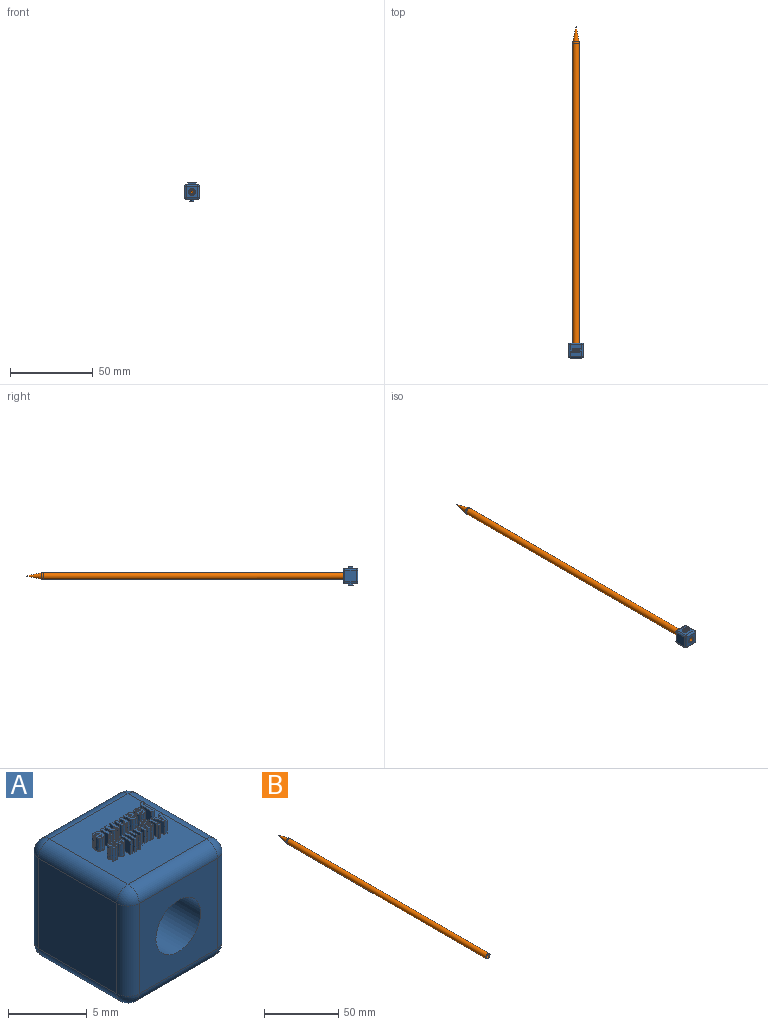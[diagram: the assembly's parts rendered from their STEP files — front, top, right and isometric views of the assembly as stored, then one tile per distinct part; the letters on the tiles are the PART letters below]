
ASSEMBLY  parts=2 mates=1
PART A: 336 faces, bbox 9x9x11 mm
  f0: plane 7x7mm, normal (0,0,1), area 44.8mm2, adj f7,f8,f9,f10,f11,f12,f13,f14
  f1: plane 7x7mm, normal (0,0,-1), area 44.5mm2, adj f136,f140,f141,f142,f162,f163,f164,f165
  f2: plane 7x7mm, normal (-1,0,0), area 49mm2, adj f141,f150,f151,f155
  f3: plane 7x7mm, normal (1,0,0), area 49mm2, adj f136,f139,f143,f144
  f4: plane 7x7mm, normal (0,-1,0), area 36.4mm2, adj f6,f139,f140,f149,f150
  f5: plane 7x7mm, normal (0,1,0), area 36.4mm2, adj f6,f142,f143,f151,f152
  f6: cylinder r=2mm len=9mm, axis (0,-1,0), area 113.1mm2, adj f4,f5
  f7: extruded ~1x0.12mm, area 0.1mm2, adj f0,f8,f16,f17
  f8: extruded ~1x0.22mm, area 0.2mm2, adj f0,f7,f9,f17
  f9: extruded ~1x0.25mm, area 0.3mm2, adj f0,f8,f10,f17
  f10: plane 1x0.87mm, normal (-1,0,0), area 0.9mm2, adj f0,f9,f11,f17
  f11: plane 1x0.2mm, normal (0,-1,0), area 0.2mm2, adj f0,f10,f12,f17
  f12: plane 1x0.87mm, normal (1,0,0), area 0.9mm2, adj f0,f11,f13,f17
  f13: extruded ~1x0.13mm, area 0.1mm2, adj f0,f12,f14,f17
  f14: extruded ~1x0.09mm, area 0.1mm2, adj f0,f13,f15,f17
  f15: extruded ~1x0.09mm, area 0.1mm2, adj f0,f14,f16,f17
  f16: plane 1x0.16mm, normal (1,0,0), area 0.2mm2, adj f0,f7,f15,f17
  f17: plane 1.21x0.41mm, normal (0,0,1), area 0.3mm2, adj f7,f8,f9,f10,f11,f12,f13,f14
  f18: extruded ~1x0.27mm, area 0.3mm2, adj f0,f19,f37,f38
  f19: extruded ~1x0.14mm, area 0.1mm2, adj f0,f18,f20,f38
  f20: extruded ~1x0.11mm, area 0.1mm2, adj f0,f19,f21,f38
  f21: plane 1x0.15mm, normal (-1,0,0), area 0.2mm2, adj f0,f20,f22,f38
  f22: extruded ~1x0.12mm, area 0.1mm2, adj f0,f21,f23,f38
  f23: extruded ~1x0.12mm, area 0.1mm2, adj f0,f22,f24,f38
  f24: extruded ~1x0.13mm, area 0.1mm2, adj f0,f23,f25,f38
  f25: extruded ~1x0.13mm, area 0.1mm2, adj f0,f24,f26,f38
  f26: plane 1x0.46mm, normal (0,1,0), area 0.5mm2, adj f0,f25,f27,f38
  f27: plane 1x0.09mm, normal (-1,0,0), area 0.1mm2, adj f0,f26,f28,f38
  f28: extruded ~1x0.24mm, area 0.3mm2, adj f0,f27,f29,f38
  f29: extruded ~1x0.24mm, area 0.3mm2, adj f0,f28,f30,f38
  f30: extruded ~1x0.25mm, area 0.3mm2, adj f0,f29,f31,f38
  f31: extruded ~1x0.28mm, area 0.3mm2, adj f0,f30,f37,f38
  f32: extruded ~1x0.1mm, area 0.1mm2, adj f33,f36,f38,f39
  f33: extruded ~1x0.1mm, area 0.1mm2, adj f32,f34,f38,f39
  f34: extruded ~1x0.11mm, area 0.1mm2, adj f33,f35,f38,f39
  f35: plane 1x0.27mm, normal (0,-1,0), area 0.3mm2, adj f34,f36,f38,f39
  f36: extruded ~1x0.11mm, area 0.1mm2, adj f32,f35,f38,f39
  f37: extruded ~1x0.27mm, area 0.3mm2, adj f0,f18,f31,f38
  f38: plane 0.74x0.66mm, normal (0,0,1), area 0.3mm2, adj f18,f19,f20,f21,f22,f23,f24,f25
  f39: plane 0.27x0.15mm, normal (0,0,1), area 0mm2, adj f32,f33,f34,f35,f36
  f40: plane 1x0.08mm, normal (-0.04,1,0), area 0.1mm2, adj f41,f64,f65,f66
  f41: plane 1x0.06mm, normal (1,0,0), area 0.1mm2, adj f40,f42,f65,f66
  f42: extruded ~1x0.1mm, area 0.1mm2, adj f41,f43,f65,f66
  f43: extruded ~1x0.11mm, area 0.1mm2, adj f42,f44,f65,f66
  f44: extruded ~1x0.09mm, area 0.1mm2, adj f43,f45,f65,f66
  f45: extruded ~1x0.09mm, area 0.1mm2, adj f44,f64,f65,f66
  f46: plane 1x0.1mm, normal (0.93,0.36,0), area 0.1mm2, adj f0,f47,f63,f65
  f47: plane 1x0.14mm, normal (0,1,0), area 0.1mm2, adj f0,f46,f48,f65
  f48: plane 1x0.47mm, normal (-1,0,0), area 0.5mm2, adj f0,f47,f49,f65
  f49: extruded ~1x0.19mm, area 0.2mm2, adj f0,f48,f50,f65
  f50: extruded ~1x0.22mm, area 0.2mm2, adj f0,f49,f51,f65
  f51: extruded ~1x0.27mm, area 0.3mm2, adj f0,f50,f52,f65
  f52: plane 1x0.13mm, normal (0.9,0.44,0), area 0.1mm2, adj f0,f51,f53,f65
  f53: extruded ~1x0.2mm, area 0.2mm2, adj f0,f52,f54,f65
  f54: extruded ~1x0.11mm, area 0.2mm2, adj f0,f53,f55,f65
  f55: plane 1x0.03mm, normal (1,0,0), area 0mm2, adj f0,f54,f56,f65
  f56: plane 1x0.12mm, normal (0.03,-1,0), area 0.1mm2, adj f0,f55,f57,f65
  f57: extruded ~1x0.24mm, area 0.2mm2, adj f0,f56,f58,f65
  f58: extruded ~1x0.17mm, area 0.2mm2, adj f0,f57,f59,f65
  f59: extruded ~1x0.17mm, area 0.2mm2, adj f0,f58,f60,f65
  f60: extruded ~1x0.16mm, area 0.2mm2, adj f0,f59,f61,f65
  f61: extruded ~1x0.14mm, area 0.1mm2, adj f0,f60,f62,f65
  f62: extruded ~1x0.1mm, area 0.1mm2, adj f0,f61,f63,f65
  f63: plane 1x0.01mm, normal (0,1,0), area 0mm2, adj f0,f46,f62,f65
  f64: extruded ~1x0.13mm, area 0.1mm2, adj f40,f45,f65,f66
  f65: plane 0.74x0.64mm, normal (0,0,1), area 0.3mm2, adj f40,f41,f42,f43,f44,f45,f46,f47
  f66: plane 0.24x0.2mm, normal (0,0,1), area 0mm2, adj f40,f41,f42,f43,f44,f45,f64
  f67: plane 1x0.19mm, normal (0,1,0), area 0.2mm2, adj f0,f68,f83,f84
  f68: plane 1x0.46mm, normal (-1,0,0), area 0.5mm2, adj f0,f67,f69,f84
  f69: extruded ~1x0.19mm, area 0.2mm2, adj f0,f68,f70,f84
  f70: extruded ~1x0.19mm, area 0.2mm2, adj f0,f69,f71,f84
  f71: extruded ~1x0.13mm, area 0.1mm2, adj f0,f70,f72,f84
  f72: extruded ~1x0.09mm, area 0.1mm2, adj f0,f71,f73,f84
  f73: plane 1x0.01mm, normal (0,-1,0), area 0mm2, adj f0,f72,f74,f84
  f74: plane 1x0.09mm, normal (-0.96,-0.28,0), area 0.1mm2, adj f0,f73,f75,f84
  f75: plane 1x0.15mm, normal (0,-1,0), area 0.1mm2, adj f0,f74,f76,f84
  f76: plane 1x0.71mm, normal (1,0,0), area 0.7mm2, adj f0,f75,f77,f84
  f77: plane 1x0.19mm, normal (0,1,0), area 0.2mm2, adj f0,f76,f78,f84
  f78: plane 1x0.34mm, normal (-1,0,0), area 0.3mm2, adj f0,f77,f79,f84
  f79: extruded ~1x0.18mm, area 0.2mm2, adj f0,f78,f80,f84
  f80: extruded ~1x0.12mm, area 0.1mm2, adj f0,f79,f81,f84
  f81: extruded ~1x0.09mm, area 0.1mm2, adj f0,f80,f82,f84
  f82: extruded ~1x0.12mm, area 0.1mm2, adj f0,f81,f83,f84
  f83: plane 1x0.42mm, normal (1,0,0), area 0.4mm2, adj f0,f67,f82,f84
  f84: plane 0.73x0.66mm, normal (0,0,1), area 0.3mm2, adj f67,f68,f69,f70,f71,f72,f73,f74
  f85: plane 1x0.19mm, normal (0,1,0), area 0.2mm2, adj f0,f86,f101,f102
  f86: plane 1x0.46mm, normal (-1,0,0), area 0.5mm2, adj f0,f85,f87,f102
  f87: extruded ~1x0.19mm, area 0.2mm2, adj f0,f86,f88,f102
  f88: extruded ~1x0.19mm, area 0.2mm2, adj f0,f87,f89,f102
  f89: extruded ~1x0.13mm, area 0.1mm2, adj f0,f88,f90,f102
  f90: extruded ~1x0.09mm, area 0.1mm2, adj f0,f89,f91,f102
  f91: plane 1x0.01mm, normal (0,-1,0), area 0mm2, adj f0,f90,f92,f102
  f92: plane 1x0.09mm, normal (-0.96,-0.28,0), area 0.1mm2, adj f0,f91,f93,f102
  f93: plane 1x0.15mm, normal (0,-1,0), area 0.1mm2, adj f0,f92,f94,f102
  f94: plane 1x0.71mm, normal (1,0,0), area 0.7mm2, adj f0,f93,f95,f102
  f95: plane 1x0.19mm, normal (0,1,0), area 0.2mm2, adj f0,f94,f96,f102
  f96: plane 1x0.34mm, normal (-1,0,0), area 0.3mm2, adj f0,f95,f97,f102
  f97: extruded ~1x0.18mm, area 0.2mm2, adj f0,f96,f98,f102
  f98: extruded ~1x0.12mm, area 0.1mm2, adj f0,f97,f99,f102
  f99: extruded ~1x0.09mm, area 0.1mm2, adj f0,f98,f100,f102
  f100: extruded ~1x0.12mm, area 0.1mm2, adj f0,f99,f101,f102
  f101: plane 1x0.42mm, normal (1,0,0), area 0.4mm2, adj f0,f85,f100,f102
  f102: plane 0.73x0.66mm, normal (0,0,1), area 0.3mm2, adj f85,f86,f87,f88,f89,f90,f91,f92
  f103: extruded ~1x0.11mm, area 0.2mm2, adj f0,f104,f107,f108
  f104: extruded ~1x0.11mm, area 0.2mm2, adj f0,f103,f105,f108
  f105: extruded ~1x0.08mm, area 0.1mm2, adj f0,f104,f106,f108
  f106: extruded ~1x0.07mm, area 0.1mm2, adj f0,f105,f107,f108
  f107: extruded ~1x0.11mm, area 0.2mm2, adj f0,f103,f106,f108
  f108: plane 0.21x0.19mm, normal (0,0,1), area 0mm2, adj f103,f104,f105,f106,f107
  f109: plane 1x0.19mm, normal (0,1,0), area 0.2mm2, adj f0,f110,f112,f113
  f110: plane 1x0.71mm, normal (-1,0,0), area 0.7mm2, adj f0,f109,f111,f113
  f111: plane 1x0.19mm, normal (0,-1,0), area 0.2mm2, adj f0,f110,f112,f113
  f112: plane 1x0.71mm, normal (1,0,0), area 0.7mm2, adj f0,f109,f111,f113
  f113: plane 0.71x0.19mm, normal (0,0,1), area 0.1mm2, adj f109,f110,f111,f112
  f114: extruded ~1x0.27mm, area 0.3mm2, adj f0,f115,f133,f134
  f115: extruded ~1x0.14mm, area 0.1mm2, adj f0,f114,f116,f134
  f116: extruded ~1x0.11mm, area 0.1mm2, adj f0,f115,f117,f134
  f117: plane 1x0.15mm, normal (-1,0,0), area 0.2mm2, adj f0,f116,f118,f134
  f118: extruded ~1x0.12mm, area 0.1mm2, adj f0,f117,f119,f134
  f119: extruded ~1x0.12mm, area 0.1mm2, adj f0,f118,f120,f134
  f120: extruded ~1x0.13mm, area 0.1mm2, adj f0,f119,f121,f134
  f121: extruded ~1x0.13mm, area 0.1mm2, adj f0,f120,f122,f134
  f122: plane 1x0.46mm, normal (0,1,0), area 0.5mm2, adj f0,f121,f123,f134
  f123: plane 1x0.09mm, normal (-1,0,0), area 0.1mm2, adj f0,f122,f124,f134
  f124: extruded ~1x0.24mm, area 0.3mm2, adj f0,f123,f125,f134
  f125: extruded ~1x0.24mm, area 0.3mm2, adj f0,f124,f126,f134
  f126: extruded ~1x0.25mm, area 0.3mm2, adj f0,f125,f127,f134
  f127: extruded ~1x0.28mm, area 0.3mm2, adj f0,f126,f133,f134
  f128: extruded ~1x0.1mm, area 0.1mm2, adj f129,f132,f134,f135
  f129: extruded ~1x0.1mm, area 0.1mm2, adj f128,f130,f134,f135
  f130: extruded ~1x0.11mm, area 0.1mm2, adj f129,f131,f134,f135
  f131: plane 1x0.27mm, normal (0,-1,0), area 0.3mm2, adj f130,f132,f134,f135
  f132: extruded ~1x0.11mm, area 0.1mm2, adj f128,f131,f134,f135
  f133: extruded ~1x0.27mm, area 0.3mm2, adj f0,f114,f127,f134
  f134: plane 0.74x0.66mm, normal (0,0,1), area 0.3mm2, adj f114,f115,f116,f117,f118,f119,f120,f121
  f135: plane 0.27x0.15mm, normal (0,0,1), area 0mm2, adj f128,f129,f130,f131,f132
  f136: cylinder r=1mm len=7mm, axis (0,-1,0), area 11mm2, adj f1,f3,f137,f138
  f137: sphere r=1mm, area 1.6mm2, adj f136,f139,f140
  f138: sphere r=1mm, area 1.6mm2, adj f136,f142,f143
  f139: cylinder r=1mm len=7mm, axis (0,0,-1), area 11mm2, adj f3,f4,f137,f145
  f140: cylinder r=1mm len=7mm, axis (-1,0,0), area 11mm2, adj f1,f4,f137,f146
  f141: cylinder r=1mm len=7mm, axis (0,1,0), area 11mm2, adj f1,f2,f146,f147
  f142: cylinder r=1mm len=7mm, axis (1,0,0), area 11mm2, adj f1,f5,f138,f147
  f143: cylinder r=1mm len=7mm, axis (0,0,1), area 11mm2, adj f3,f5,f138,f148
  f144: cylinder r=1mm len=7mm, axis (0,1,0), area 11mm2, adj f0,f3,f145,f148
  f145: sphere r=1mm, area 1.6mm2, adj f139,f144,f149
  f146: sphere r=1mm, area 1.6mm2, adj f140,f141,f150
  f147: sphere r=1mm, area 1.6mm2, adj f141,f142,f151
  f148: sphere r=1mm, area 1.6mm2, adj f143,f144,f152
  f149: cylinder r=1mm len=7mm, axis (1,0,0), area 11mm2, adj f0,f4,f145,f153
  f150: cylinder r=1mm len=7mm, axis (0,0,1), area 11mm2, adj f2,f4,f146,f153
  f151: cylinder r=1mm len=7mm, axis (0,0,-1), area 11mm2, adj f2,f5,f147,f154
  f152: cylinder r=1mm len=7mm, axis (-1,0,0), area 11mm2, adj f0,f5,f148,f154
  f153: sphere r=1mm, area 1.6mm2, adj f149,f150,f155
  f154: sphere r=1mm, area 1.6mm2, adj f151,f152,f155
  f155: cylinder r=1mm len=7mm, axis (0,-1,0), area 11mm2, adj f0,f2,f153,f154
  f156: plane 1x0.55mm, normal (-1,0,0), area 0.6mm2, adj f157,f173,f174,f175
  f157: plane 1x0.78mm, normal (0,-1,0), area 0.8mm2, adj f156,f158,f174,f175
  f158: plane 1x0.9mm, normal (0.83,0.55,0), area 1.1mm2, adj f157,f159,f174,f175
  f159: extruded ~1x0.36mm, area 0.4mm2, adj f158,f160,f174,f175
  f160: plane 1x0.02mm, normal (0,1,0), area 0mm2, adj f159,f161,f174,f175
  f161: extruded ~1x0.3mm, area 0.3mm2, adj f160,f173,f174,f175
  f162: plane 1x0.39mm, normal (0,1,0), area 0.4mm2, adj f1,f163,f172,f174
  f163: plane 1x0.53mm, normal (1,0,0), area 0.5mm2, adj f1,f162,f164,f174
  f164: plane 1x0.39mm, normal (0,-1,0), area 0.4mm2, adj f1,f163,f165,f174
  f165: plane 2.04x1mm, normal (1,0,0), area 2mm2, adj f1,f164,f166,f174
  f166: plane 1x0.63mm, normal (0,-1,0), area 0.6mm2, adj f1,f165,f167,f174
  f167: plane 2.1x1.42mm, normal (-0.83,-0.56,0), area 2.5mm2, adj f1,f166,f168,f174
  f168: plane 1x0.48mm, normal (-1,0,0), area 0.5mm2, adj f1,f167,f169,f174
  f169: plane 1.39x1mm, normal (0,1,0), area 1.4mm2, adj f1,f168,f170,f174
  f170: plane 1x0.67mm, normal (-1,0,0), area 0.7mm2, adj f1,f169,f171,f174
  f171: plane 1x0.67mm, normal (0,1,0), area 0.7mm2, adj f1,f170,f172,f174
  f172: plane 1x0.67mm, normal (1,0,0), area 0.7mm2, adj f1,f162,f171,f174
  f173: extruded ~1x0.4mm, area 0.4mm2, adj f156,f161,f174,f175
  f174: plane 3.25x2.45mm, normal (0,0,-1), area 4mm2, adj f156,f157,f158,f159,f160,f161,f162,f163
  f175: plane 1.25x0.81mm, normal (0,0,-1), area 0.5mm2, adj f156,f157,f158,f159,f160,f161,f173
  f176: extruded ~1x0.31mm, area 0.3mm2, adj f177,f187,f188,f189
  f177: plane 1x0.22mm, normal (0,-1,0), area 0.2mm2, adj f176,f178,f188,f189
  f178: extruded ~1x0.36mm, area 0.4mm2, adj f177,f187,f188,f189
  f179: plane 1x0.2mm, normal (0.96,0.29,0), area 0.2mm2, adj f0,f180,f186,f188
  f180: plane 1x0.19mm, normal (0,1,0), area 0.2mm2, adj f0,f179,f181,f188
  f181: plane 1x0.84mm, normal (-0.94,-0.33,0), area 0.9mm2, adj f0,f180,f182,f188
  f182: plane 1x0.22mm, normal (0,-1,0), area 0.2mm2, adj f0,f181,f183,f188
  f183: plane 1x0.84mm, normal (0.94,-0.33,0), area 0.9mm2, adj f0,f182,f184,f188
  f184: plane 1x0.19mm, normal (0,1,0), area 0.2mm2, adj f0,f183,f185,f188
  f185: plane 1x0.2mm, normal (-0.96,0.29,0), area 0.2mm2, adj f0,f184,f186,f188
  f186: plane 1x0.31mm, normal (0,1,0), area 0.3mm2, adj f0,f179,f185,f188
  f187: extruded ~1x0.06mm, area 0.1mm2, adj f176,f178,f188,f189
  f188: plane 0.84x0.81mm, normal (0,0,1), area 0.3mm2, adj f176,f177,f178,f179,f180,f181,f182,f183
  f189: plane 0.36x0.22mm, normal (0,0,1), area 0mm2, adj f176,f177,f178,f187
  f190: extruded ~1x0.1mm, area 0.1mm2, adj f0,f191,f194,f195
  f191: extruded ~1x0.1mm, area 0.1mm2, adj f0,f190,f192,f195
  f192: extruded ~1x0.07mm, area 0.1mm2, adj f0,f191,f193,f195
  f193: extruded ~1x0.06mm, area 0.1mm2, adj f0,f192,f194,f195
  f194: extruded ~1x0.1mm, area 0.1mm2, adj f0,f190,f193,f195
  f195: plane 0.19x0.17mm, normal (0,0,1), area 0mm2, adj f190,f191,f192,f193,f194
  f196: plane 1x0.18mm, normal (0,1,0), area 0.2mm2, adj f0,f197,f199,f200
  f197: plane 1x0.64mm, normal (-1,0,0), area 0.6mm2, adj f0,f196,f198,f200
  f198: plane 1x0.18mm, normal (0,-1,0), area 0.2mm2, adj f0,f197,f199,f200
  f199: plane 1x0.64mm, normal (1,0,0), area 0.6mm2, adj f0,f196,f198,f200
  f200: plane 0.64x0.18mm, normal (0,0,1), area 0.1mm2, adj f196,f197,f198,f199
  f201: extruded ~1x0.08mm, area 0.1mm2, adj f202,f244,f245,f246
  f202: extruded ~1x0.12mm, area 0.2mm2, adj f201,f203,f245,f246
  f203: extruded ~1x0.12mm, area 0.2mm2, adj f202,f204,f245,f246
  f204: extruded ~1x0.08mm, area 0.1mm2, adj f203,f205,f245,f246
  f205: extruded ~1x0.07mm, area 0.1mm2, adj f204,f244,f245,f246
  f206: extruded ~1x0.06mm, area 0.1mm2, adj f207,f242,f245,f247
  f207: extruded ~1x0.06mm, area 0.1mm2, adj f206,f208,f245,f247
  f208: extruded ~1x0.08mm, area 0.1mm2, adj f207,f209,f245,f247
  f209: plane 1x0.09mm, normal (0,1,0), area 0.1mm2, adj f208,f210,f245,f247
  f210: extruded ~1x0.1mm, area 0.1mm2, adj f209,f211,f245,f247
  f211: extruded ~1x0.05mm, area 0.1mm2, adj f210,f212,f245,f247
  f212: extruded ~1x0.07mm, area 0.1mm2, adj f211,f213,f245,f247
  f213: extruded ~1x0.15mm, area 0.2mm2, adj f212,f242,f245,f247
  f214: plane 1x0.09mm, normal (-1,0,0), area 0.1mm2, adj f0,f215,f243,f245
  f215: plane 1x0.22mm, normal (0,-1,0), area 0.2mm2, adj f0,f214,f216,f245
  f216: extruded ~1x0.05mm, area 0mm2, adj f0,f215,f217,f245
  f217: extruded ~1x0.06mm, area 0.1mm2, adj f0,f216,f218,f245
  f218: extruded ~1x0.2mm, area 0.2mm2, adj f0,f217,f219,f245
  f219: extruded ~1x0.16mm, area 0.2mm2, adj f0,f218,f220,f245
  f220: extruded ~1x0.11mm, area 0.1mm2, adj f0,f219,f221,f245
  f221: extruded ~1x0.08mm, area 0.1mm2, adj f0,f220,f222,f245
  f222: extruded ~1x0.06mm, area 0.1mm2, adj f0,f221,f223,f245
  f223: extruded ~1x0.06mm, area 0.1mm2, adj f0,f222,f224,f245
  f224: extruded ~1x0.06mm, area 0.1mm2, adj f0,f223,f225,f245
  f225: extruded ~1x0.05mm, area 0.1mm2, adj f0,f224,f226,f245
  f226: extruded ~1x0.11mm, area 0.1mm2, adj f0,f225,f227,f245
  f227: extruded ~1x0.1mm, area 0.1mm2, adj f0,f226,f228,f245
  f228: extruded ~1x0.13mm, area 0.2mm2, adj f0,f227,f229,f245
  f229: extruded ~1x0.21mm, area 0.2mm2, adj f0,f228,f230,f245
  f230: extruded ~1x0.27mm, area 0.3mm2, adj f0,f229,f231,f245
  f231: extruded ~1x0.18mm, area 0.2mm2, adj f0,f230,f232,f245
  f232: extruded ~1x0.13mm, area 0.1mm2, adj f0,f231,f233,f245
  f233: extruded ~1x0.16mm, area 0.2mm2, adj f0,f232,f234,f245
  f234: plane 1x0.11mm, normal (0,-1,0), area 0.1mm2, adj f0,f233,f235,f245
  f235: extruded ~1x0.1mm, area 0.1mm2, adj f0,f234,f236,f245
  f236: extruded ~1x0.05mm, area 0.1mm2, adj f0,f235,f237,f245
  f237: plane 1x0.03mm, normal (0.11,0.99,0), area 0mm2, adj f0,f236,f238,f245
  f238: plane 1x0.03mm, normal (0.06,1,0), area 0mm2, adj f0,f237,f239,f245
  f239: extruded ~1x0.2mm, area 0.2mm2, adj f0,f238,f240,f245
  f240: extruded ~1x0.16mm, area 0.2mm2, adj f0,f239,f241,f245
  f241: extruded ~1x0.1mm, area 0.1mm2, adj f0,f240,f243,f245
  f242: extruded ~1x0.1mm, area 0.1mm2, adj f206,f213,f245,f247
  f243: plane 1x0.1mm, normal (-0.25,0.97,0), area 0.1mm2, adj f0,f214,f241,f245
  f244: extruded ~1x0.07mm, area 0.1mm2, adj f201,f205,f245,f246
  f245: plane 0.94x0.65mm, normal (0,0,1), area 0.4mm2, adj f201,f202,f203,f204,f205,f206,f207,f208
  f246: plane 0.23x0.19mm, normal (0,0,1), area 0mm2, adj f201,f202,f203,f204,f205,f244
  f247: plane 0.33x0.16mm, normal (0,0,1), area 0mm2, adj f206,f207,f208,f209,f210,f211,f212,f213
  f248: plane 1x0.08mm, normal (0.96,0.28,0), area 0.1mm2, adj f0,f249,f264,f265
  f249: plane 1x0.13mm, normal (0,1,0), area 0.1mm2, adj f0,f248,f250,f265
  f250: plane 1x0.64mm, normal (-1,0,0), area 0.6mm2, adj f0,f249,f251,f265
  f251: plane 1x0.18mm, normal (0,-1,0), area 0.2mm2, adj f0,f250,f252,f265
  f252: plane 1x0.3mm, normal (1,0,0), area 0.3mm2, adj f0,f251,f253,f265
  f253: extruded ~1x0.16mm, area 0.2mm2, adj f0,f252,f254,f265
  f254: extruded ~1x0.11mm, area 0.1mm2, adj f0,f253,f255,f265
  f255: extruded ~1x0.08mm, area 0.1mm2, adj f0,f254,f256,f265
  f256: extruded ~1x0.1mm, area 0.1mm2, adj f0,f255,f257,f265
  f257: plane 1x0.38mm, normal (-1,0,0), area 0.4mm2, adj f0,f256,f258,f265
  f258: plane 1x0.18mm, normal (0,-1,0), area 0.2mm2, adj f0,f257,f259,f265
  f259: plane 1x0.42mm, normal (1,0,0), area 0.4mm2, adj f0,f258,f260,f265
  f260: extruded ~1x0.17mm, area 0.2mm2, adj f0,f259,f261,f265
  f261: extruded ~1x0.17mm, area 0.2mm2, adj f0,f260,f262,f265
  f262: extruded ~1x0.12mm, area 0.1mm2, adj f0,f261,f263,f265
  f263: extruded ~1x0.08mm, area 0.1mm2, adj f0,f262,f264,f265
  f264: plane 1x0.01mm, normal (0,1,0), area 0mm2, adj f0,f248,f263,f265
  f265: plane 0.65x0.59mm, normal (0,0,1), area 0.3mm2, adj f248,f249,f250,f251,f252,f253,f254,f255
  f266: extruded ~1x0.1mm, area 0.1mm2, adj f0,f267,f270,f271
  f267: extruded ~1x0.1mm, area 0.1mm2, adj f0,f266,f268,f271
  f268: extruded ~1x0.07mm, area 0.1mm2, adj f0,f267,f269,f271
  f269: extruded ~1x0.06mm, area 0.1mm2, adj f0,f268,f270,f271
  f270: extruded ~1x0.1mm, area 0.1mm2, adj f0,f266,f269,f271
  f271: plane 0.19x0.17mm, normal (0,0,1), area 0mm2, adj f266,f267,f268,f269,f270
  f272: plane 1x0.18mm, normal (0,1,0), area 0.2mm2, adj f0,f273,f275,f276
  f273: plane 1x0.64mm, normal (-1,0,0), area 0.6mm2, adj f0,f272,f274,f276
  f274: plane 1x0.18mm, normal (0,-1,0), area 0.2mm2, adj f0,f273,f275,f276
  f275: plane 1x0.64mm, normal (1,0,0), area 0.6mm2, adj f0,f272,f274,f276
  f276: plane 0.64x0.18mm, normal (0,0,1), area 0.1mm2, adj f272,f273,f274,f275
  f277: plane 1x0.18mm, normal (0,1,0), area 0.2mm2, adj f0,f278,f280,f281
  f278: plane 1x0.89mm, normal (-1,0,0), area 0.9mm2, adj f0,f277,f279,f281
  f279: plane 1x0.18mm, normal (0,-1,0), area 0.2mm2, adj f0,f278,f280,f281
  f280: plane 1x0.89mm, normal (1,0,0), area 0.9mm2, adj f0,f277,f279,f281
  f281: plane 0.89x0.18mm, normal (0,0,1), area 0.2mm2, adj f277,f278,f279,f280
  f282: plane 1x0.18mm, normal (0,1,0), area 0.2mm2, adj f0,f283,f285,f286
  f283: plane 1x0.89mm, normal (-1,0,0), area 0.9mm2, adj f0,f282,f284,f286
  f284: plane 1x0.18mm, normal (0,-1,0), area 0.2mm2, adj f0,f283,f285,f286
  f285: plane 1x0.89mm, normal (1,0,0), area 0.9mm2, adj f0,f282,f284,f286
  f286: plane 0.89x0.18mm, normal (0,0,1), area 0.2mm2, adj f282,f283,f284,f285
  f287: extruded ~1x0.24mm, area 0.3mm2, adj f0,f288,f306,f307
  f288: extruded ~1x0.13mm, area 0.1mm2, adj f0,f287,f289,f307
  f289: extruded ~1x0.1mm, area 0.1mm2, adj f0,f288,f290,f307
  f290: plane 1x0.14mm, normal (-1,0,0), area 0.1mm2, adj f0,f289,f291,f307
  f291: extruded ~1x0.11mm, area 0.1mm2, adj f0,f290,f292,f307
  f292: extruded ~1x0.11mm, area 0.1mm2, adj f0,f291,f293,f307
  f293: extruded ~1x0.12mm, area 0.1mm2, adj f0,f292,f294,f307
  f294: extruded ~1x0.12mm, area 0.1mm2, adj f0,f293,f295,f307
  f295: plane 1x0.41mm, normal (0,1,0), area 0.4mm2, adj f0,f294,f296,f307
  f296: plane 1x0.09mm, normal (-1,0,0), area 0.1mm2, adj f0,f295,f297,f307
  f297: extruded ~1x0.21mm, area 0.2mm2, adj f0,f296,f298,f307
  f298: extruded ~1x0.21mm, area 0.2mm2, adj f0,f297,f299,f307
  f299: extruded ~1x0.22mm, area 0.2mm2, adj f0,f298,f300,f307
  f300: extruded ~1x0.25mm, area 0.3mm2, adj f0,f299,f306,f307
  f301: extruded ~1x0.09mm, area 0.1mm2, adj f302,f305,f307,f308
  f302: extruded ~1x0.09mm, area 0.1mm2, adj f301,f303,f307,f308
  f303: extruded ~1x0.1mm, area 0.1mm2, adj f302,f304,f307,f308
  f304: plane 1x0.25mm, normal (0,-1,0), area 0.2mm2, adj f303,f305,f307,f308
  f305: extruded ~1x0.1mm, area 0.1mm2, adj f301,f304,f307,f308
  f306: extruded ~1x0.24mm, area 0.3mm2, adj f0,f287,f300,f307
  f307: plane 0.67x0.59mm, normal (0,0,1), area 0.2mm2, adj f287,f288,f289,f290,f291,f292,f293,f294
  f308: plane 0.25x0.14mm, normal (0,0,1), area 0mm2, adj f301,f302,f303,f304,f305
  f309: extruded ~1x0.15mm, area 0.2mm2, adj f0,f310,f334,f335
  f310: extruded ~1x0.08mm, area 0.1mm2, adj f0,f309,f311,f335
  f311: extruded ~1x0.06mm, area 0.1mm2, adj f0,f310,f312,f335
  f312: extruded ~1x0.11mm, area 0.1mm2, adj f0,f311,f313,f335
  f313: extruded ~1x0.11mm, area 0.1mm2, adj f0,f312,f314,f335
  f314: extruded ~1x0.04mm, area 0mm2, adj f0,f313,f315,f335
  f315: extruded ~1x0.08mm, area 0.1mm2, adj f0,f314,f316,f335
  f316: extruded ~1x0.09mm, area 0.1mm2, adj f0,f315,f317,f335
  f317: extruded ~1x0.09mm, area 0.1mm2, adj f0,f316,f318,f335
  f318: plane 1x0.13mm, normal (-0.92,0.39,0), area 0.1mm2, adj f0,f317,f319,f335
  f319: extruded ~1x0.23mm, area 0.2mm2, adj f0,f318,f320,f335
  f320: extruded ~1x0.19mm, area 0.2mm2, adj f0,f319,f321,f335
  f321: extruded ~1x0.13mm, area 0.2mm2, adj f0,f320,f322,f335
  f322: extruded ~1x0.08mm, area 0.1mm2, adj f0,f321,f323,f335
  f323: extruded ~1x0.06mm, area 0.1mm2, adj f0,f322,f324,f335
  f324: extruded ~1x0.11mm, area 0.1mm2, adj f0,f323,f325,f335
  f325: extruded ~1x0.08mm, area 0.1mm2, adj f0,f324,f326,f335
  f326: extruded ~1x0.04mm, area 0.1mm2, adj f0,f325,f327,f335
  f327: extruded ~1x0.03mm, area 0mm2, adj f0,f326,f328,f335
  f328: extruded ~1x0.1mm, area 0.1mm2, adj f0,f327,f329,f335
  f329: extruded ~1x0.11mm, area 0.1mm2, adj f0,f328,f330,f335
  f330: extruded ~1x0.11mm, area 0.1mm2, adj f0,f329,f331,f335
  f331: plane 1x0.14mm, normal (1,0,0), area 0.1mm2, adj f0,f330,f332,f335
  f332: extruded ~1x0.09mm, area 0.1mm2, adj f0,f331,f333,f335
  f333: extruded ~1x0.12mm, area 0.1mm2, adj f0,f332,f334,f335
  f334: extruded ~1x0.21mm, area 0.2mm2, adj f0,f309,f333,f335
  f335: plane 0.67x0.49mm, normal (0,0,1), area 0.2mm2, adj f309,f310,f311,f312,f313,f314,f315,f316
PART B: 8 faces, bbox 4x200x4 mm
  f0: cylinder r=1.5mm len=190mm, axis (0,1,0), area 1790.7mm2, adj f2,f4
  f1: cylinder r=2mm len=189.51mm, axis (0,1,0), area 2381.4mm2, adj f2,f5
  f2: plane 4x4mm, normal (0,-1,0), area 5.5mm2, adj f0,f1
  f3: cone r=2mm half-angle=11.3deg, axis (0,-1,0), area 58mm2, adj f5
  f4: plane 3x3mm, normal (0,-1,0), area 4.1mm2, adj f0,f6
  f5: revolved ~4x4mm, area 12.2mm2, adj f1,f3
  f6: revolved ~1.94x1.94mm, area 1.7mm2, adj f4,f7
  f7: cone r=1.02mm half-angle=11.3deg, axis (0,-1,0), area 13.6mm2, adj f6
PLACE A t=(-5.81,2.82,2.51)mm fixed
PLACE B t=(-5.81,183.82,2.51)mm
MATE fastened A.f6 <-> B.f1  axis (0,-1,0) through (-5.81,-6.18,2.51)mm
